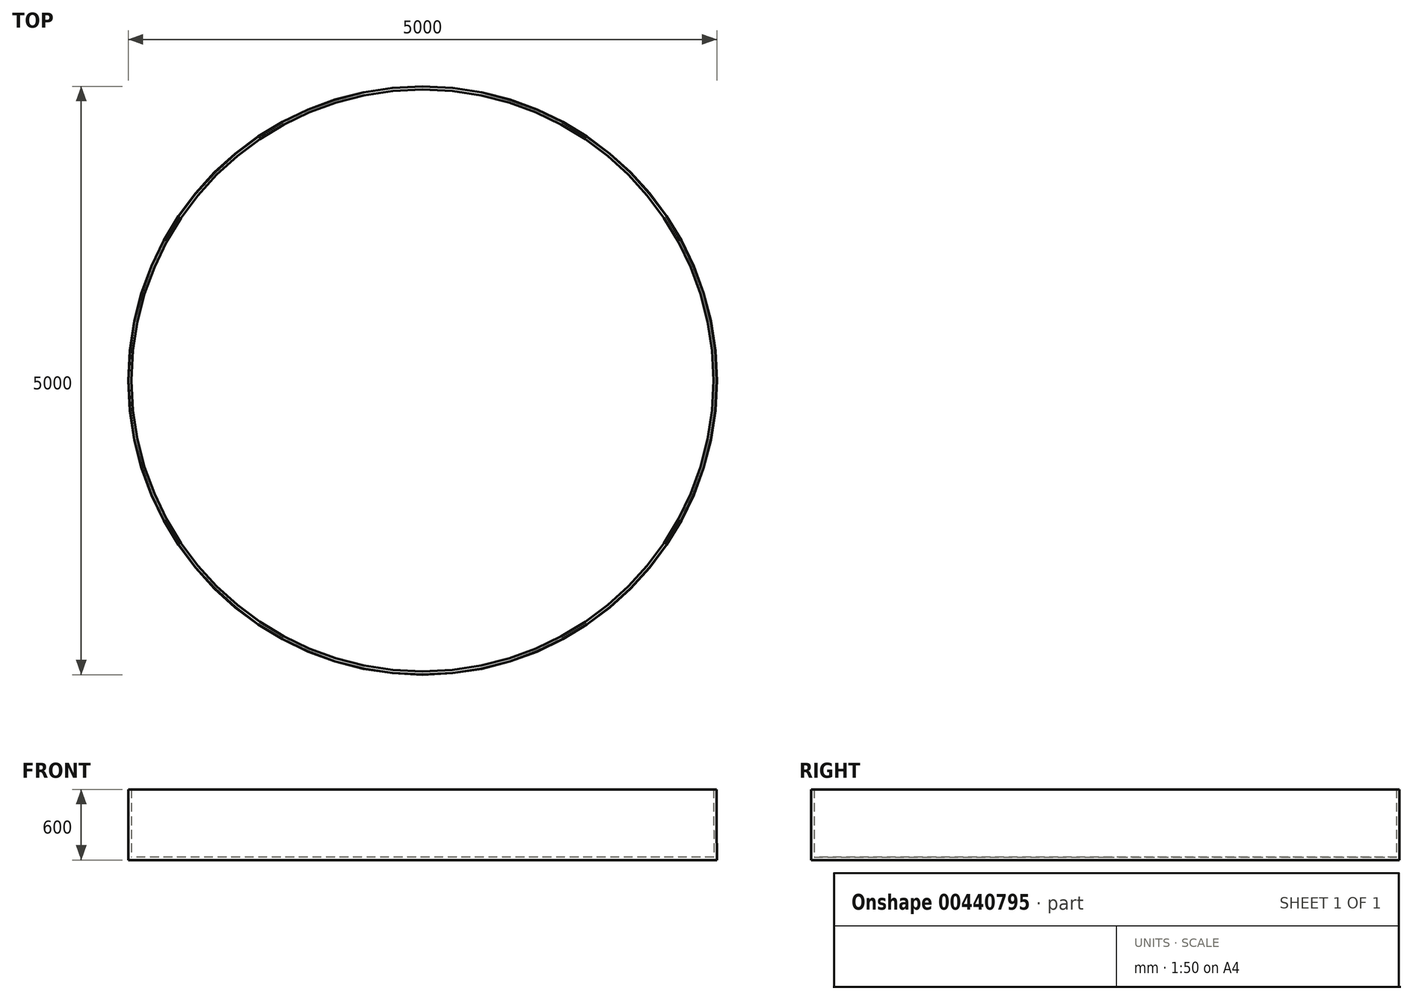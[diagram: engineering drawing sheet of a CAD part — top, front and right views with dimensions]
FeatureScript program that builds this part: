
annotation { "Feature Type Name" : "Feature", "Feature Type Description" : "" }
export const myFeature = defineFeature(function(context is Context, id is Id, definition is map)
    precondition{}
    {
        {
            var Q0;
            Q0=qCreatedBy(makeId("Top.planeOp"),FACE);
            var sketch = newSketch(context, id + "F0", { "sketchPlane" : qUnion([Q0])});
            skCircle(sketch, "E0", {"center": v(0, 0) * mm, "radius": 2500 * mm});
            skSolve(sketch);
        }
        {
            var Q0;
            Q0=qSketchRegion(id+"F0",true);
            extrude(context, id + "F1", {"entities" : qUnion([Q0]), "depth" : 600 * mm, "hasDraft" : true, "draftAngle" : .2 * degree, "draftPullDirection" : true});
        }
        {
            var Q0;
            Q0=makeQuery(id+"F1.opExtrude","CAP_FACE",FACE,{"disambiguationData":[OSD([sQuery(id+"F0.wireOp",EDGE,"E0")])],"isStart":false});
            shell(context, id + "F2", {"entities" : qUnion([Q0]), "thickness" : 25 * mm});
        }
    });
